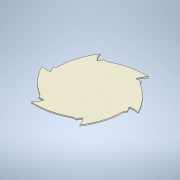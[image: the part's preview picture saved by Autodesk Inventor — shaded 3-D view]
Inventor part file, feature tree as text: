
AUTODESK INVENTOR PART (.ipt)
format: ipt  version: 2021 (Build 250183000, 183)  size: 151,040 bytes
history: native  units: mm
features: extrude x1, sketch x1
ambient origin geometry x8: Origin, YZ Plane, XZ Plane, XY Plane, X Axis, Y Axis, Z Axis, Center Point
bodies: Solid1 (feature_tree)
feature tree (2):
  extrude  "Extrusion1"  Depth=1.7mm TaperAngle=0.0deg
  sketch  "Sketch1"  dims[d0=101.0mm d1=1.7mm d2=0.0mm d17=60.0mm d19=360.0deg d21=24.545793mm d22=97.275208mm d23=4.976467mm d24=7.689824mm]
